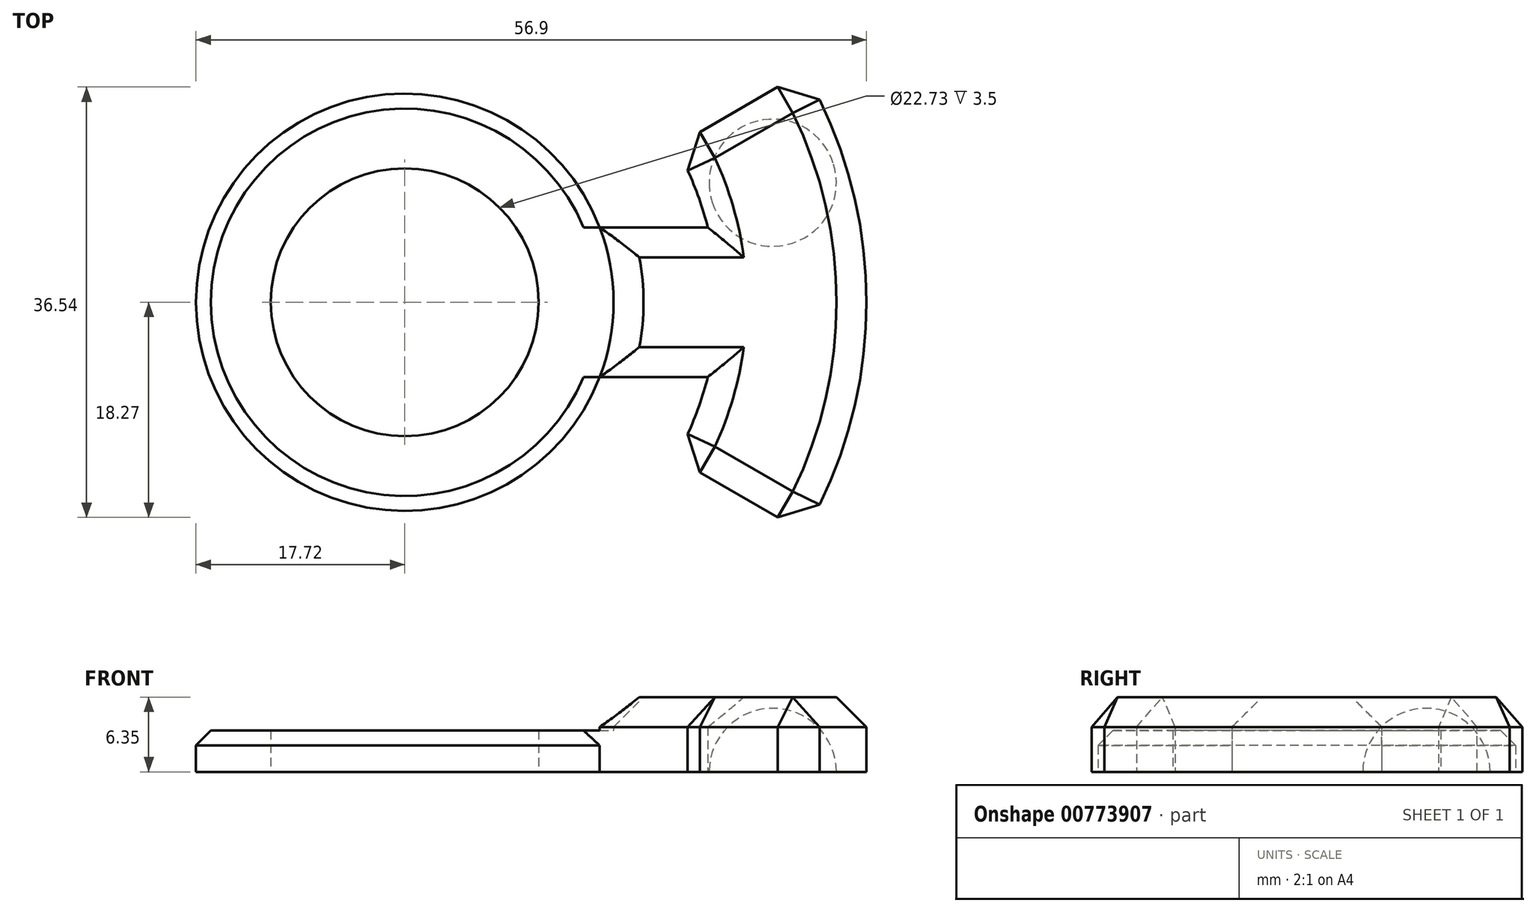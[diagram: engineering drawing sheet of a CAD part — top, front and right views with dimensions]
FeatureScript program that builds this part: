
annotation { "Feature Type Name" : "Feature", "Feature Type Description" : "" }
export const myFeature = defineFeature(function(context is Context, id is Id, definition is map)
    precondition{}
    {
        {
            var Q0;
            Q0=qCreatedBy(makeId("Front.planeOp"),FACE);
            var sketch = newSketch(context, id + "F0", { "sketchPlane" : qUnion([Q0])});
            skLineSegment(sketch, "E0", {"start": v(0, 5.84) * mm, "end": v(0, -5.84) * mm, "construction": true});
            skSolve(sketch);
        }
        {
            var Q0;
            Q0=qCreatedBy(makeId("Top.planeOp"),FACE);
            var sketch = newSketch(context, id + "F1", { "sketchPlane" : qUnion([Q0])});
            skCircle(sketch, "E1", {"center": v(0, 0) * mm, "radius": 11.37 * mm});
            skCircle(sketch, "E2", {"center": v(0, 0) * mm, "radius": 17.72 * mm});
            skSolve(sketch);
        }
        {
            var Q0;
            Q0=qSketchRegion(id+"F1",true);
            extrude(context, id + "F2", {"entities" : qUnion([Q0]), "depth" : 7 * mm, "offsetDistance" : 25.4 * mm, "symmetric" : true});
        }
        {
            var Q0;
            Q0=qCreatedBy(makeId("Top.planeOp"),FACE);
            var sketch = newSketch(context, id + "F3", { "sketchPlane" : qUnion([Q0])});
            skArc(sketch, "E3.0", {"start": v(16.54, -6.35) * mm, "mid": v(17.72, 0) * mm, "end": v(16.54, 6.35) * mm});
            skLineSegment(sketch, "E4", {"start": v(16.54, 6.35) * mm, "end": v(25.7, 6.35) * mm});
            skLineSegment(sketch, "E5", {"start": v(16.54, -6.35) * mm, "end": v(25.7, -6.35) * mm});
            skLineSegment(sketch, "E6", {"start": v(0, 0) * mm, "end": v(39.18, 0) * mm, "construction": true});
            skArc(sketch, "E7", {"start": v(25.7, 6.35) * mm, "mid": v(24.56, 9.9) * mm, "end": v(22.93, 13.24) * mm});
            skArc(sketch, "E8", {"start": v(25.7, -6.35) * mm, "mid": v(24.56, -9.9) * mm, "end": v(22.93, -13.24) * mm});
            skArc(sketch, "E9", {"start": v(33.93, -19.59) * mm, "mid": v(39.18, 0) * mm, "end": v(33.93, 19.59) * mm});
            skLineSegment(sketch, "E10", {"start": v(22.93, 13.24) * mm, "end": v(33.93, 19.59) * mm});
            skLineSegment(sketch, "E11", {"start": v(22.93, -13.24) * mm, "end": v(33.93, -19.59) * mm});
            skPoint(sketch, "E12", {"position": v(39.18, 0) * mm});
            skLineSegment(sketch, "E13", {"start": v(0, 0) * mm, "end": v(33.93, 19.59) * mm, "construction": true});
            skSolve(sketch);
        }
        {
            var Q0;
            Q0=qSketchRegion(id+"F3",true);
            extrude(context, id + "F4", {"entities" : qUnion([Q0]), "operationType" : NewBodyOperationType.ADD, "depth" : 12.7 * mm, "offsetDistance" : 25.4 * mm, "symmetric" : true});
        }
        {
            var Q0;
            Q0=sQuery(id+"F0.wireOp",EDGE,"E0");
            var Q1;
            Q1=qCreatedBy(makeId("Front.planeOp"),FACE);
            cPlane(context, id + "F5", {"entities" : qUnion([Q0, Q1]), "cplaneType" : CPlaneType.LINE_ANGLE, "offset" : 6.35 * mm, "angle" : 18 * degree, "oppositeDirection" : true, "width" : 152.4 * mm, "height" : 152.4 * mm});
        }
        {
            var Q0;
            Q0=qCreatedBy(id+"F5.planeOp",FACE);
            var sketch = newSketch(context, id + "F6", { "sketchPlane" : qUnion([Q0])});
            skArc(sketch, "E14", {"start": v(-27.43, 0) * mm, "mid": v(-32.83, 5.4) * mm, "end": v(-38.23, 0) * mm});
            skLineSegment(sketch, "E15", {"start": v(-38.23, 0) * mm, "end": v(-27.43, 0) * mm});
            skLineSegment(sketch, "E16", {"start": v(-27.43, 0) * mm, "end": v(0, 0) * mm, "construction": true});
            skPoint(sketch, "E17", {"position": v(-39.18, 0) * mm});
            skPoint(sketch, "E18", {"position": v(-26.48, 0) * mm});
            skSolve(sketch);
        }
        {
            var Q0;
            Q0=qSketchRegion(id+"F6",true);
            var Q1;
            Q1=sQuery(id+"F6.wireOp",EDGE,"E16");
            revolve(context, id + "F7", {"operationType" : NewBodyOperationType.REMOVE, "surfaceOperationType" : NewSurfaceOperationType.NEW, "entities" : qUnion([Q0]), "axis" : qUnion([Q1]), "revolveType" : RevolveType.FULL, "oppositeDirection" : true});
        }
        {
            var Q0;
            Q0=makeQuery(id+"F4.opExtrude","CAP_FACE",FACE,{"disambiguationData":[OSD([sQuery(id+"F3.wireOp",EDGE,"E3.0"),sQuery(id+"F3.wireOp",EDGE,"E4"),sQuery(id+"F3.wireOp",EDGE,"E5"),sQuery(id+"F3.wireOp",EDGE,"E7"),sQuery(id+"F3.wireOp",EDGE,"E8"),sQuery(id+"F3.wireOp",EDGE,"E9"),sQuery(id+"F3.wireOp",EDGE,"E10"),sQuery(id+"F3.wireOp",EDGE,"E11")])],"isStart":false});
            var Q1;
            Q1=makeQuery(id+"F4.opExtrude","SWEPT_EDGE",EDGE,{"disambiguationData":[OSD([sQuery(id+"F3.wireOp",EDGE,"E8"),sQuery(id+"F3.wireOp",EDGE,"E11")])]});
            var Q2;
            Q2=makeQuery(id+"F4.opExtrude","SWEPT_EDGE",EDGE,{"disambiguationData":[OSD([sQuery(id+"F3.wireOp",EDGE,"E9"),sQuery(id+"F3.wireOp",EDGE,"E11")])]});
            var Q3;
            Q3=makeQuery(id+"F4.opExtrude","SWEPT_EDGE",EDGE,{"disambiguationData":[OSD([sQuery(id+"F3.wireOp",EDGE,"E9"),sQuery(id+"F3.wireOp",EDGE,"E10")])]});
            var Q4;
            Q4=makeQuery(id+"F4.opExtrude","SWEPT_EDGE",EDGE,{"disambiguationData":[OSD([sQuery(id+"F3.wireOp",EDGE,"E7"),sQuery(id+"F3.wireOp",EDGE,"E10")])]});
            var Q5;
            Q5=makeQuery(id+"F4.opExtrude","CAP_FACE",FACE,{"disambiguationData":[OSD([sQuery(id+"F3.wireOp",EDGE,"E3.0"),sQuery(id+"F3.wireOp",EDGE,"E4"),sQuery(id+"F3.wireOp",EDGE,"E5"),sQuery(id+"F3.wireOp",EDGE,"E7"),sQuery(id+"F3.wireOp",EDGE,"E8"),sQuery(id+"F3.wireOp",EDGE,"E9"),sQuery(id+"F3.wireOp",EDGE,"E10"),sQuery(id+"F3.wireOp",EDGE,"E11")])],"isStart":true});
            chamfer(context, id + "F8", {"entities" : qUnion([Q0, Q1, Q2, Q3, Q4, Q5]), "width" : 2.54 * mm, "tangentPropagation" : true});
        }
        {
            var Q0;
            {var subQ0=makeQuery(id+"F4.opExtrude","SWEPT_FACE",FACE,{"disambiguationData":[OSD([sQuery(id+"F3.wireOp",EDGE,"E5")])]});var subQ1=sQuery(id+"F3.wireOp",EDGE,"E3.0");var subQ2=makeQuery(id+"F4.opExtrude","SWEPT_FACE",FACE,{"disambiguationData":[OSD([subQ1])]});var subQ3=sQuery(id+"F1.wireOp",EDGE,"E2");var subQ4=makeQuery(id+"F2.opExtrude","CAP_FACE",FACE,{"disambiguationData":[OSD([sQuery(id+"F1.wireOp",EDGE,"E1"),subQ3])],"isStart":true});var subQ5=makeQuery(id+"F2.opExtrude","SWEPT_FACE",FACE,{"disambiguationData":[OSD([subQ3])]});Q0=makeQuery(id+"FOLW99IOsfEzG7j_1.2.F4.boolean.opBoolean","SPLIT",EDGE,{"disambiguationData":[topologyDisambiguationEdgeConnected([subQ4,subQ5]),TD([subQ2])],"derivedFrom":makeQuery(id+"FOLW99IOsfEzG7j_1.1.F4.boolean.opBoolean","SPLIT",EDGE,{"disambiguationData":[topologyDisambiguationEdgeConnected([subQ4,subQ5]),TD([subQ0])],"derivedFrom":makeQuery(id+"F4.boolean.opBoolean","SPLIT",EDGE,{"disambiguationData":[topologyDisambiguationEdgeConnected([subQ5])],"derivedFrom":makeQuery(id+"F2.opExtrude","CAP_EDGE",EDGE,{"disambiguationData":[OSD([subQ3])],"isStart":true})})})});}
            var Q1;
            {var subQ1=sQuery(id+"F1.wireOp",EDGE,"E2");var subQ2=makeQuery(id+"F2.opExtrude","CAP_FACE",FACE,{"disambiguationData":[OSD([sQuery(id+"F1.wireOp",EDGE,"E1"),subQ1])],"isStart":true});var subQ3=makeQuery(id+"F2.opExtrude","SWEPT_FACE",FACE,{"disambiguationData":[OSD([subQ1])]});Q1=makeQuery(id+"FOLW99IOsfEzG7j_1.1.F4.boolean.opBoolean","SPLIT",EDGE,{"disambiguationData":[topologyDisambiguationEdgeConnected([subQ2,subQ3]),TD([makeQuery(id+"F4.opExtrude","SWEPT_FACE",FACE,{"disambiguationData":[OSD([sQuery(id+"F3.wireOp",EDGE,"E4")])]})])],"derivedFrom":makeQuery(id+"F4.boolean.opBoolean","SPLIT",EDGE,{"disambiguationData":[topologyDisambiguationEdgeConnected([subQ3])],"derivedFrom":makeQuery(id+"F2.opExtrude","CAP_EDGE",EDGE,{"disambiguationData":[OSD([subQ1])],"isStart":true})})});}
            var Q2;
            {var subQ0=sQuery(id+"F3.wireOp",EDGE,"E3.0");var subQ1=makeQuery(id+"FOLW99IOsfEzG7j_1.1.F4.opExtrude","SWEPT_FACE",FACE,{"disambiguationData":[OSD([subQ0])]});var subQ2=sQuery(id+"F1.wireOp",EDGE,"E2");var subQ3=makeQuery(id+"F2.opExtrude","SWEPT_FACE",FACE,{"disambiguationData":[OSD([subQ2])]});var subQ5=makeQuery(id+"F2.opExtrude","CAP_FACE",FACE,{"disambiguationData":[OSD([sQuery(id+"F1.wireOp",EDGE,"E1"),subQ2])],"isStart":true});var subQ6=sQuery(id+"F3.wireOp",EDGE,"E5");Q2=makeQuery(id+"FOLW99IOsfEzG7j_1.2.F4.boolean.opBoolean","SPLIT",EDGE,{"disambiguationData":[topologyDisambiguationEdgeConnected([subQ5,subQ3]),TD([subQ1])],"derivedFrom":makeQuery(id+"FOLW99IOsfEzG7j_1.1.F4.boolean.opBoolean","SPLIT",EDGE,{"disambiguationData":[topologyDisambiguationEdgeConnected([subQ5,subQ3]),TD([makeQuery(id+"F4.opExtrude","SWEPT_FACE",FACE,{"disambiguationData":[OSD([subQ6])]})])],"derivedFrom":makeQuery(id+"F4.boolean.opBoolean","SPLIT",EDGE,{"disambiguationData":[topologyDisambiguationEdgeConnected([subQ3])],"derivedFrom":makeQuery(id+"F2.opExtrude","CAP_EDGE",EDGE,{"disambiguationData":[OSD([subQ2])],"isStart":true})})})});}
            var Q3;
            {var subQ1=sQuery(id+"F1.wireOp",EDGE,"E2");var subQ2=makeQuery(id+"F2.opExtrude","CAP_FACE",FACE,{"disambiguationData":[OSD([sQuery(id+"F1.wireOp",EDGE,"E1"),subQ1])],"isStart":false});var subQ3=sQuery(id+"F3.wireOp",EDGE,"E3.0");var subQ4=makeQuery(id+"FOLW99IOsfEzG7j_1.1.F4.opExtrude","SWEPT_FACE",FACE,{"disambiguationData":[OSD([subQ3])]});var subQ5=makeQuery(id+"F2.opExtrude","SWEPT_FACE",FACE,{"disambiguationData":[OSD([subQ1])]});var subQ6=sQuery(id+"F3.wireOp",EDGE,"E5");Q3=makeQuery(id+"FOLW99IOsfEzG7j_1.2.F4.boolean.opBoolean","SPLIT",EDGE,{"disambiguationData":[topologyDisambiguationEdgeConnected([subQ2,subQ5]),TD([subQ4])],"derivedFrom":makeQuery(id+"FOLW99IOsfEzG7j_1.1.F4.boolean.opBoolean","SPLIT",EDGE,{"disambiguationData":[topologyDisambiguationEdgeConnected([subQ2,subQ5]),TD([makeQuery(id+"F4.opExtrude","SWEPT_FACE",FACE,{"disambiguationData":[OSD([subQ6])]})])],"derivedFrom":makeQuery(id+"F4.boolean.opBoolean","SPLIT",EDGE,{"disambiguationData":[topologyDisambiguationEdgeConnected([subQ5])],"derivedFrom":makeQuery(id+"F2.opExtrude","CAP_EDGE",EDGE,{"disambiguationData":[OSD([subQ1])],"isStart":false})})})});}
            var Q4;
            {var subQ1=sQuery(id+"F1.wireOp",EDGE,"E2");var subQ2=makeQuery(id+"F2.opExtrude","SWEPT_FACE",FACE,{"disambiguationData":[OSD([subQ1])]});var subQ3=makeQuery(id+"F2.opExtrude","CAP_FACE",FACE,{"disambiguationData":[OSD([sQuery(id+"F1.wireOp",EDGE,"E1"),subQ1])],"isStart":false});Q4=makeQuery(id+"FOLW99IOsfEzG7j_1.1.F4.boolean.opBoolean","SPLIT",EDGE,{"disambiguationData":[topologyDisambiguationEdgeConnected([subQ3,subQ2]),TD([makeQuery(id+"F4.opExtrude","SWEPT_FACE",FACE,{"disambiguationData":[OSD([sQuery(id+"F3.wireOp",EDGE,"E4")])]})])],"derivedFrom":makeQuery(id+"F4.boolean.opBoolean","SPLIT",EDGE,{"disambiguationData":[topologyDisambiguationEdgeConnected([subQ2])],"derivedFrom":makeQuery(id+"F2.opExtrude","CAP_EDGE",EDGE,{"disambiguationData":[OSD([subQ1])],"isStart":false})})});}
            var Q5;
            {var subQ0=sQuery(id+"F3.wireOp",EDGE,"E3.0");var subQ1=makeQuery(id+"F4.opExtrude","SWEPT_FACE",FACE,{"disambiguationData":[OSD([subQ0])]});var subQ2=sQuery(id+"F1.wireOp",EDGE,"E2");var subQ3=makeQuery(id+"F2.opExtrude","SWEPT_FACE",FACE,{"disambiguationData":[OSD([subQ2])]});var subQ5=makeQuery(id+"F4.opExtrude","SWEPT_FACE",FACE,{"disambiguationData":[OSD([sQuery(id+"F3.wireOp",EDGE,"E5")])]});var subQ6=makeQuery(id+"F2.opExtrude","CAP_FACE",FACE,{"disambiguationData":[OSD([sQuery(id+"F1.wireOp",EDGE,"E1"),subQ2])],"isStart":false});Q5=makeQuery(id+"FOLW99IOsfEzG7j_1.2.F4.boolean.opBoolean","SPLIT",EDGE,{"disambiguationData":[topologyDisambiguationEdgeConnected([subQ6,subQ3]),TD([subQ1])],"derivedFrom":makeQuery(id+"FOLW99IOsfEzG7j_1.1.F4.boolean.opBoolean","SPLIT",EDGE,{"disambiguationData":[topologyDisambiguationEdgeConnected([subQ6,subQ3]),TD([subQ5])],"derivedFrom":makeQuery(id+"F4.boolean.opBoolean","SPLIT",EDGE,{"disambiguationData":[topologyDisambiguationEdgeConnected([subQ3])],"derivedFrom":makeQuery(id+"F2.opExtrude","CAP_EDGE",EDGE,{"disambiguationData":[OSD([subQ2])],"isStart":false})})})});}
            chamfer(context, id + "F9", {"entities" : qUnion([Q0, Q1, Q2, Q3, Q4, Q5]), "width" : 1.27 * mm, "tangentPropagation" : true});
        }
        {
            var Q0;
            Q0=qCreatedBy(makeId("Front.planeOp"),FACE);
            var sketch = newSketch(context, id + "F10", { "sketchPlane" : qUnion([Q0])});
            skLineSegment(sketch, "E19.bottom", {"start": v(-43.55, 0) * mm, "end": v(43.55, 0) * mm});
            skLineSegment(sketch, "E19.top", {"start": v(-43.55, -13.73) * mm, "end": v(43.55, -13.73) * mm});
            skLineSegment(sketch, "E19.left", {"start": v(-43.55, 0) * mm, "end": v(-43.55, -13.73) * mm});
            skLineSegment(sketch, "E19.right", {"start": v(43.55, 0) * mm, "end": v(43.55, -13.73) * mm});
            skSolve(sketch);
        }
        {
            var Q0;
            Q0=qSketchRegion(id+"F10",true);
            extrude(context, id + "F11", {"entities" : qUnion([Q0]), "operationType" : NewBodyOperationType.REMOVE, "oppositeDirection" : true, "depth" : 101.6 * mm, "offsetDistance" : 25.4 * mm, "symmetric" : true});
        }
    });
